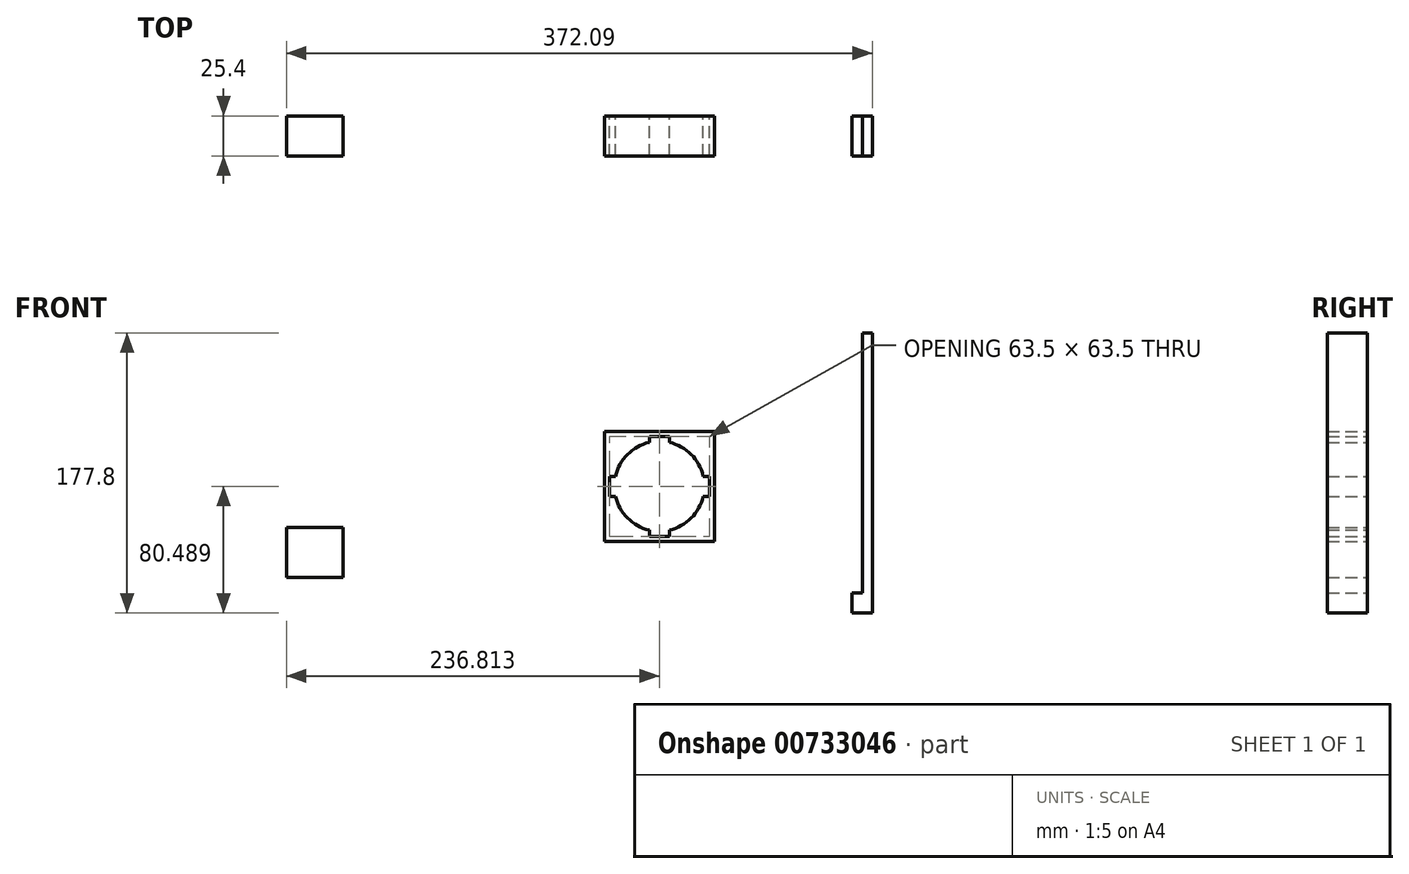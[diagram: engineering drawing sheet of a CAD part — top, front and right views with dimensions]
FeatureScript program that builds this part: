
annotation { "Feature Type Name" : "Feature", "Feature Type Description" : "" }
export const myFeature = defineFeature(function(context is Context, id is Id, definition is map)
    precondition{}
    {
        {
            var Q0;
            Q0=qCreatedBy(makeId("Front.planeOp"),FACE);
            var sketch = newSketch(context, id + "F0", { "sketchPlane" : qUnion([Q0])});
            skLineSegment(sketch, "E0.bottom", {"start": v(-198.64, 19.33) * mm, "end": v(-185.94, 19.33) * mm});
            skLineSegment(sketch, "E0.top", {"start": v(-198.64, 6.63) * mm, "end": v(-185.94, 6.63) * mm});
            skLineSegment(sketch, "E0.left", {"start": v(-198.64, 19.33) * mm, "end": v(-198.64, 6.63) * mm});
            skLineSegment(sketch, "E0.right", {"start": v(-185.94, 19.33) * mm, "end": v(-185.94, 6.63) * mm});
            skArc(sketch, "E1", {"start": v(-182.6, 0.4) * mm, "mid": v(-192.3, 28.85) * mm, "end": v(-201.99, 0.4) * mm});
            skLineSegment(sketch, "E2", {"start": v(-192.3, -34.65) * mm, "end": v(-163.72, -34.65) * mm});
            skLineSegment(sketch, "E3", {"start": v(-192.3, -34.65) * mm, "end": v(-220.87, -34.65) * mm});
            skLineSegment(sketch, "E4", {"start": v(-198.64, 6.63) * mm, "end": v(-220.87, -34.65) * mm});
            skLineSegment(sketch, "E5", {"start": v(-185.94, 6.63) * mm, "end": v(-163.72, -34.65) * mm});
            skLineSegment(sketch, "E6", {"start": v(-220.87, 12.98) * mm, "end": v(-220.87, 70.13) * mm});
            skLineSegment(sketch, "E7", {"start": v(-163.72, 70.13) * mm, "end": v(-163.72, 12.98) * mm});
            skLineSegment(sketch, "E8.left", {"start": v(-220.87, 70.13) * mm, "end": v(-220.87, 60.6) * mm});
            skLineSegment(sketch, "E9.left", {"start": v(-163.72, 70.13) * mm, "end": v(-163.72, 60.6) * mm});
            skLineSegment(sketch, "E10", {"start": v(-220.87, 70.13) * mm, "end": v(-211.34, 60.6) * mm});
            skLineSegment(sketch, "E11", {"start": v(-173.24, 60.6) * mm, "end": v(-163.72, 70.13) * mm});
            skLineSegment(sketch, "E12", {"start": v(-211.34, 60.6) * mm, "end": v(-173.24, 60.6) * mm});
            skPoint(sketch, "E13.orphan", {"position": v(-192.3, 19.33) * mm});
            skPoint(sketch, "E14.end.orphan", {"position": v(-192.3, 6.63) * mm});
            skLineSegment(sketch, "E15", {"start": v(-192.3, 60.6) * mm, "end": v(-192.3, -34.65) * mm});
            skLineSegment(sketch, "E16", {"start": v(-163.72, 12.98) * mm, "end": v(-175.62, -12.54) * mm});
            skLineSegment(sketch, "E17", {"start": v(-220.87, 12.98) * mm, "end": v(-208.96, -12.54) * mm});
            skLineSegment(sketch, "E18.bottom", {"start": v(-121.05, -117.53) * mm, "end": v(-51.2, -117.53) * mm});
            skLineSegment(sketch, "E18.top", {"start": v(-121.05, -187.38) * mm, "end": v(-51.2, -187.38) * mm});
            skLineSegment(sketch, "E18.left", {"start": v(-121.05, -117.53) * mm, "end": v(-121.05, -146.1) * mm});
            skLineSegment(sketch, "E18.right", {"start": v(-51.2, -117.53) * mm, "end": v(-51.2, -187.38) * mm});
            skLineSegment(sketch, "E19", {"start": v(-86.13, -117.53) * mm, "end": v(-86.13, -120.7) * mm, "construction": true});
            skLineSegment(sketch, "E20", {"start": v(-121.05, -152.45) * mm, "end": v(-117.88, -152.45) * mm, "construction": true});
            skArc(sketch, "E21", {"start": v(-113.99, -158.8) * mm, "mid": v(-106.33, -172.66) * mm, "end": v(-92.48, -180.31) * mm});
            skLineSegment(sketch, "E22", {"start": v(-117.52, -146.1) * mm, "end": v(-113.99, -146.1) * mm});
            skLineSegment(sketch, "E23", {"start": v(-117.52, -158.8) * mm, "end": v(-113.99, -158.8) * mm});
            skLineSegment(sketch, "E24", {"start": v(-86.13, -117.53) * mm, "end": v(-92.48, -117.53) * mm});
            skLineSegment(sketch, "E25", {"start": v(-86.13, -117.53) * mm, "end": v(-79.78, -117.53) * mm});
            skArc(sketch, "E26.trimOffspring", {"start": v(-92.48, -124.6) * mm, "mid": v(-106.33, -132.25) * mm, "end": v(-113.99, -146.1) * mm});
            skLineSegment(sketch, "E27", {"start": v(-92.48, -124.6) * mm, "end": v(-92.48, -121.06) * mm});
            skLineSegment(sketch, "E28", {"start": v(-79.78, -124.6) * mm, "end": v(-79.78, -121.06) * mm});
            skLineSegment(sketch, "E29.trimOffspring", {"start": v(-121.05, -158.8) * mm, "end": v(-121.05, -187.38) * mm});
            skLineSegment(sketch, "E30", {"start": v(-121.05, -146.1) * mm, "end": v(-121.05, -158.8) * mm});
            skLineSegment(sketch, "E31", {"start": v(-51.2, -152.45) * mm, "end": v(-51.2, -146.1) * mm});
            skLineSegment(sketch, "E32", {"start": v(-54.73, -146.1) * mm, "end": v(-58.27, -146.1) * mm});
            skLineSegment(sketch, "E33", {"start": v(-51.2, -152.45) * mm, "end": v(-51.2, -158.8) * mm});
            skLineSegment(sketch, "E34", {"start": v(-54.73, -158.8) * mm, "end": v(-58.27, -158.8) * mm});
            skLineSegment(sketch, "E35", {"start": v(-86.13, -187.38) * mm, "end": v(-92.48, -187.38) * mm});
            skLineSegment(sketch, "E36", {"start": v(-92.48, -183.84) * mm, "end": v(-92.48, -180.31) * mm});
            skLineSegment(sketch, "E37", {"start": v(-86.13, -187.38) * mm, "end": v(-79.78, -187.38) * mm});
            skLineSegment(sketch, "E38", {"start": v(-79.78, -183.84) * mm, "end": v(-79.78, -180.31) * mm});
            skLineSegment(sketch, "E39", {"start": v(-220.87, -34.65) * mm, "end": v(-220.87, -56.66) * mm});
            skArc(sketch, "E40.trimOffspring", {"start": v(-79.78, -180.31) * mm, "mid": v(-65.92, -172.66) * mm, "end": v(-58.27, -158.8) * mm});
            skArc(sketch, "E41.trimOffspring", {"start": v(-58.27, -146.1) * mm, "mid": v(-65.92, -132.25) * mm, "end": v(-79.78, -124.6) * mm});
            skLineSegment(sketch, "E42", {"start": v(-117.88, -152.45) * mm, "end": v(-117.88, -146.1) * mm});
            skLineSegment(sketch, "E43", {"start": v(-117.88, -146.1) * mm, "end": v(-117.52, -146.1) * mm});
            skLineSegment(sketch, "E44", {"start": v(-117.88, -152.45) * mm, "end": v(-117.88, -158.8) * mm});
            skLineSegment(sketch, "E45", {"start": v(-117.88, -158.8) * mm, "end": v(-117.52, -158.8) * mm});
            skLineSegment(sketch, "E46.trimOffspring", {"start": v(-114.7, -152.45) * mm, "end": v(-51.2, -152.45) * mm, "construction": true});
            skLineSegment(sketch, "E47.MirrorCS", {"start": v(-54.38, -152.45) * mm, "end": v(-54.38, -146.1) * mm});
            skLineSegment(sketch, "E48.MirrorCS", {"start": v(-54.38, -152.45) * mm, "end": v(-54.38, -158.8) * mm});
            skLineSegment(sketch, "E49", {"start": v(-54.38, -146.1) * mm, "end": v(-54.73, -146.1) * mm});
            skLineSegment(sketch, "E50", {"start": v(-54.38, -158.8) * mm, "end": v(-54.73, -158.8) * mm});
            skLineSegment(sketch, "E51", {"start": v(-86.13, -123.88) * mm, "end": v(-86.13, -120.7) * mm});
            skLineSegment(sketch, "E52", {"start": v(-86.13, -120.7) * mm, "end": v(-79.78, -120.7) * mm});
            skLineSegment(sketch, "E53", {"start": v(-79.78, -120.7) * mm, "end": v(-79.78, -121.06) * mm});
            skLineSegment(sketch, "E54", {"start": v(-86.13, -120.7) * mm, "end": v(-92.48, -120.7) * mm});
            skLineSegment(sketch, "E55", {"start": v(-92.48, -120.7) * mm, "end": v(-92.48, -121.06) * mm});
            skLineSegment(sketch, "E56.trimOffspring", {"start": v(-86.13, -123.88) * mm, "end": v(-86.13, -187.38) * mm, "construction": true});
            skLineSegment(sketch, "E57.MirrorCS", {"start": v(-86.13, -184.2) * mm, "end": v(-92.48, -184.2) * mm});
            skLineSegment(sketch, "E58.MirrorCS", {"start": v(-86.13, -184.2) * mm, "end": v(-79.78, -184.2) * mm});
            skLineSegment(sketch, "E59", {"start": v(-92.48, -183.84) * mm, "end": v(-92.48, -184.2) * mm});
            skLineSegment(sketch, "E60", {"start": v(-79.78, -183.84) * mm, "end": v(-79.78, -184.2) * mm});
            skLineSegment(sketch, "E61.bottom", {"start": v(36.07, -232.94) * mm, "end": v(49.15, -232.94) * mm});
            skLineSegment(sketch, "E61.top", {"start": v(36.07, -220.24) * mm, "end": v(42.8, -220.24) * mm});
            skLineSegment(sketch, "E61.left", {"start": v(36.07, -232.94) * mm, "end": v(36.07, -220.24) * mm});
            skLineSegment(sketch, "E61.right", {"start": v(49.15, -232.94) * mm, "end": v(49.15, -220.24) * mm});
            skLineSegment(sketch, "E62.top", {"start": v(49.15, -55.14) * mm, "end": v(42.8, -55.14) * mm});
            skLineSegment(sketch, "E62.left", {"start": v(49.15, -220.24) * mm, "end": v(49.15, -55.14) * mm});
            skLineSegment(sketch, "E62.right", {"start": v(42.8, -220.24) * mm, "end": v(42.8, -55.14) * mm});
            skLineSegment(sketch, "E63.bottom", {"start": v(28.58, -0.8) * mm, "end": v(-28.58, -0.8) * mm});
            skLineSegment(sketch, "E63.top", {"start": v(28.58, 0.8) * mm, "end": v(-28.58, 0.8) * mm});
            skLineSegment(sketch, "E63.left", {"start": v(28.58, -0.8) * mm, "end": v(28.58, 0.8) * mm});
            skLineSegment(sketch, "E63.right", {"start": v(-28.58, -0.8) * mm, "end": v(-28.58, 0.8) * mm});
            skPoint(sketch, "E63.middle", {"position": v(0, 0) * mm});
            skLineSegment(sketch, "E64.bottom", {"start": v(-0.8, 28.58) * mm, "end": v(0.8, 28.58) * mm});
            skLineSegment(sketch, "E64.top", {"start": v(-0.8, -28.58) * mm, "end": v(0.8, -28.58) * mm});
            skLineSegment(sketch, "E64.left", {"start": v(-0.8, 28.58) * mm, "end": v(-0.8, -28.58) * mm});
            skLineSegment(sketch, "E64.right", {"start": v(0.8, 28.58) * mm, "end": v(0.8, -28.58) * mm});
            skCircle(sketch, "E65", {"center": v(0, 0) * mm, "radius": 19.05 * mm});
            skLineSegment(sketch, "E66", {"start": v(28.58, -0.8) * mm, "end": v(26.97, -0.8) * mm, "construction": true});
            skLineSegment(sketch, "E67", {"start": v(0.8, -28.58) * mm, "end": v(0.8, -26.97) * mm, "construction": true});
            skLineSegment(sketch, "E68", {"start": v(0.8, -26.97) * mm, "end": v(26.97, -0.8) * mm});
            skLineSegment(sketch, "E69", {"start": v(28.58, 0.8) * mm, "end": v(26.2, 0.8) * mm, "construction": true});
            skLineSegment(sketch, "E70", {"start": v(0.8, 28.58) * mm, "end": v(0.8, 26.19) * mm, "construction": true});
            skLineSegment(sketch, "E71", {"start": v(0.8, 26.19) * mm, "end": v(26.2, 0.8) * mm});
            skLineSegment(sketch, "E72", {"start": v(-0.8, 28.58) * mm, "end": v(-28.58, 0.8) * mm});
            skLineSegment(sketch, "E73.bottom", {"start": v(-287.03, -210.42) * mm, "end": v(-322.94, -210.42) * mm});
            skLineSegment(sketch, "E73.top", {"start": v(-287.03, -178.67) * mm, "end": v(-322.94, -178.67) * mm});
            skLineSegment(sketch, "E73.left", {"start": v(-287.03, -210.42) * mm, "end": v(-287.03, -178.67) * mm});
            skLineSegment(sketch, "E73.right", {"start": v(-322.94, -210.42) * mm, "end": v(-322.94, -178.67) * mm});
            skPoint(sketch, "E73.middle", {"position": v(-304.99, -194.54) * mm});
            skSolve(sketch);
        }
        {
            var Q0;
            {var subQ11=sQuery(id+"F0.wireOp",EDGE,"E18.left");Q0=makeQuery(id+"F0.imprint","IMPRINT",FACE,{"disambiguationData":[TD([[makeQuery(id+"F0.imprint","IMPRINT",EDGE,{"derivedFrom":subQ11}),1.0]])]});}
            var Q1;
            Q1=makeQuery(id+"F0.imprint","IMPRINT",FACE,{"disambiguationData":[TD([[makeQuery(id+"F0.imprint","IMPRINT",EDGE,{"derivedFrom":sQuery(id+"F0.wireOp",EDGE,"E61.bottom")}),1.0]])]});
            var Q2;
            Q2=makeQuery(id+"F0.imprint","IMPRINT",FACE,{"disambiguationData":[TD([[makeQuery(id+"F0.imprint","IMPRINT",EDGE,{"derivedFrom":sQuery(id+"F0.wireOp",EDGE,"E73.bottom")}),-1.0]])]});
            extrude(context, id + "F1", {"entities" : qUnion([Q0, Q1, Q2]), "depth" : 25.4 * mm, "offsetDistance" : 25.4 * mm});
        }
    });
